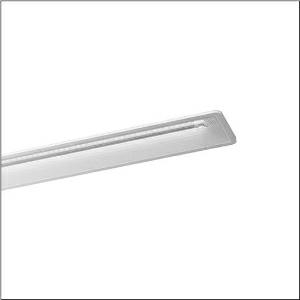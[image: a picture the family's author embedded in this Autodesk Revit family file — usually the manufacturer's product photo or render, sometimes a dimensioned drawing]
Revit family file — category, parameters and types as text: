
# Revit family: taris_r__21_5mt116d03wd_9457
name_source: partatom
category: Lighting Fixtures
units: mm (PartAtom-declared; Revit-internal decimal feet)

## family parameters
Cut with Voids When Loaded = No
Host = Face
Light Source = No
Part Type = Normal
Room Calculation Point = No
Round Connector Dimension = Use Diameter
Shared = No

## types (1)
- --- (1 x LED, 4560 lm, 28.9 W, 3000K)
    Apparent Load = 29 VA
    CIE Flux Codes = 73 96 99 100 100
    Color Rendering = 80
    Color Temperature = 3000K
    Default Elevation = 1800 mm
    Description = Taris® 21, office luminaire, primary anti-glare with micro louvre, primary optical cover: axial lens, of PMMA, structured, CAT 2 (L<= 1500cd/m²), light emission: direct distribution, primary light characteristic: symmetric, installation type: recessed, LED rated luminous flux: 4.560 lm, light colour: 830, colour temperature: 3000K, control gear: ECG DALI, with terminal, 5-pole, mains connection: 230V, AC, 50Hz, rated input power: 29W, housing, luminaire housing, of plastic, traffic white (RAL 9016), module: M625, length: 1.250 mm, width: 150 mm, height: 76mm, recess depth: 106 mm, protection rating (complete): IP20, insulation class (complete): insulation class I (protective earthing), certification: CE, ENEC, VDE, protection symbol: F, impact resistance: IK02, permissible ambient temperature for indoor applications: 0..+35°C, standard: EN 50419, packaging unit: 1 piece
    Height = 0 mm  [stored 0 ft]
    Lamp = 1 x LED
    Lamp Light Flux = 4560 lm
    Lamp Power = 28.9 W
    Lamp count = 1
    Length = 1243 mm
    Luminous efficacy = 158 lm/W
    Manufacturer = Siteco
    ModVariant = No
    Model = 5MT116D03WD
    Mounting Place = Ceiling
    Mounting Type = Recessed
    Number of Poles = 1
    OnlyDefault = Yes
    Power Factor = 1
    Product Name = Taris® 21
    Product group = office luminaire | ceiling recessed
    ProductGroupID = 400
    Protection Class = Protection class I
    Protection Degree = IP 20
    RLX_Detail_Level = 1
    RlxData = <blob elided: 29977 chars, md5=3612371b>
    Socket = socket
    Standby Power = 0 W
    System Light Flux = 4560 lm
    System Power = 29 W
    Type Comments = factory setting: luminous flux: 100 % | dim-lin: 254 | 200 mA
    Type Image = l_1004723.jpg
    URL = http://relux.com
    VarID = @adj_130193
    Voltage = 0 V
    Weight = 0.00 kg
    Width = 144 mm

note: [stored X ft] marks values corroborated as IEEE doubles in the binary element streams (Revit-internal decimal feet)

## geometry (parser evidence)
native form markers: Blend x4, Sweep x9
no freeform markers — native parametric forms only
